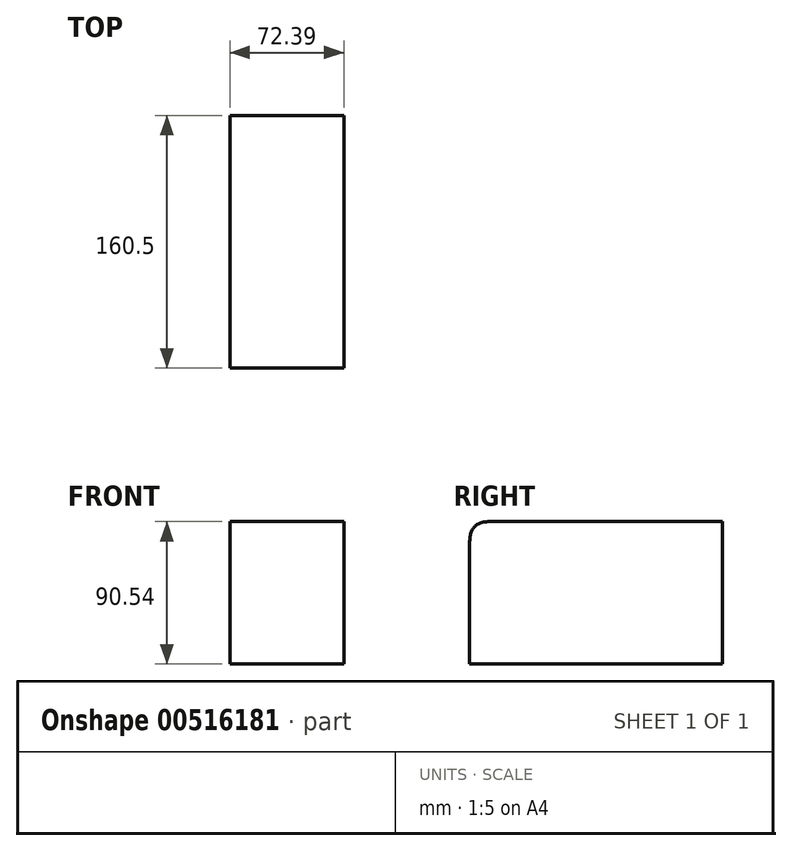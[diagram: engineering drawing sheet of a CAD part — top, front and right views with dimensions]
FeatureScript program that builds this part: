
annotation { "Feature Type Name" : "Feature", "Feature Type Description" : "" }
export const myFeature = defineFeature(function(context is Context, id is Id, definition is map)
    precondition{}
    {
        {
            var Q0;
            Q0=qCreatedBy(makeId("Right.planeOp"),FACE);
            var sketch = newSketch(context, id + "F0", { "sketchPlane" : qUnion([Q0])});
            skLineSegment(sketch, "E0.bottom", {"start": v(80.25, -45.27) * mm, "end": v(-80.25, -45.27) * mm});
            skLineSegment(sketch, "E0.top", {"start": v(80.25, 45.27) * mm, "end": v(-80.25, 45.27) * mm});
            skLineSegment(sketch, "E0.left", {"start": v(80.25, -45.27) * mm, "end": v(80.25, 45.27) * mm});
            skLineSegment(sketch, "E0.right", {"start": v(-80.25, -45.27) * mm, "end": v(-80.25, 45.27) * mm});
            skPoint(sketch, "E0.middle", {"position": v(0, 0) * mm});
            skSolve(sketch);
        }
        {
            var Q0;
            Q0 = qSketchRegion(id + "F0", true);
            extrude(context, id + "F1", {"entities" : qUnion([Q0]), "depth" : 72.39 * mm, "offsetDistance" : 25.4 * mm});
        }
        {
            var Q0;
            Q0=makeQuery(id+"F1.opExtrude","SWEPT_EDGE",EDGE,{"disambiguationData":[OSD([sQuery(id+"F0.wireOp",EDGE,"E0.top"),sQuery(id+"F0.wireOp",EDGE,"E0.right")])]});
            fillet(context, id + "F2", {"entities" : qUnion([Q0]), "radius" : 12.7 * mm, "tangentPropagation" : true, "rho" : 0.5, "crossSection" : FilletCrossSection.CONIC, "allowEdgeOverflow" : false});
        }
    });
